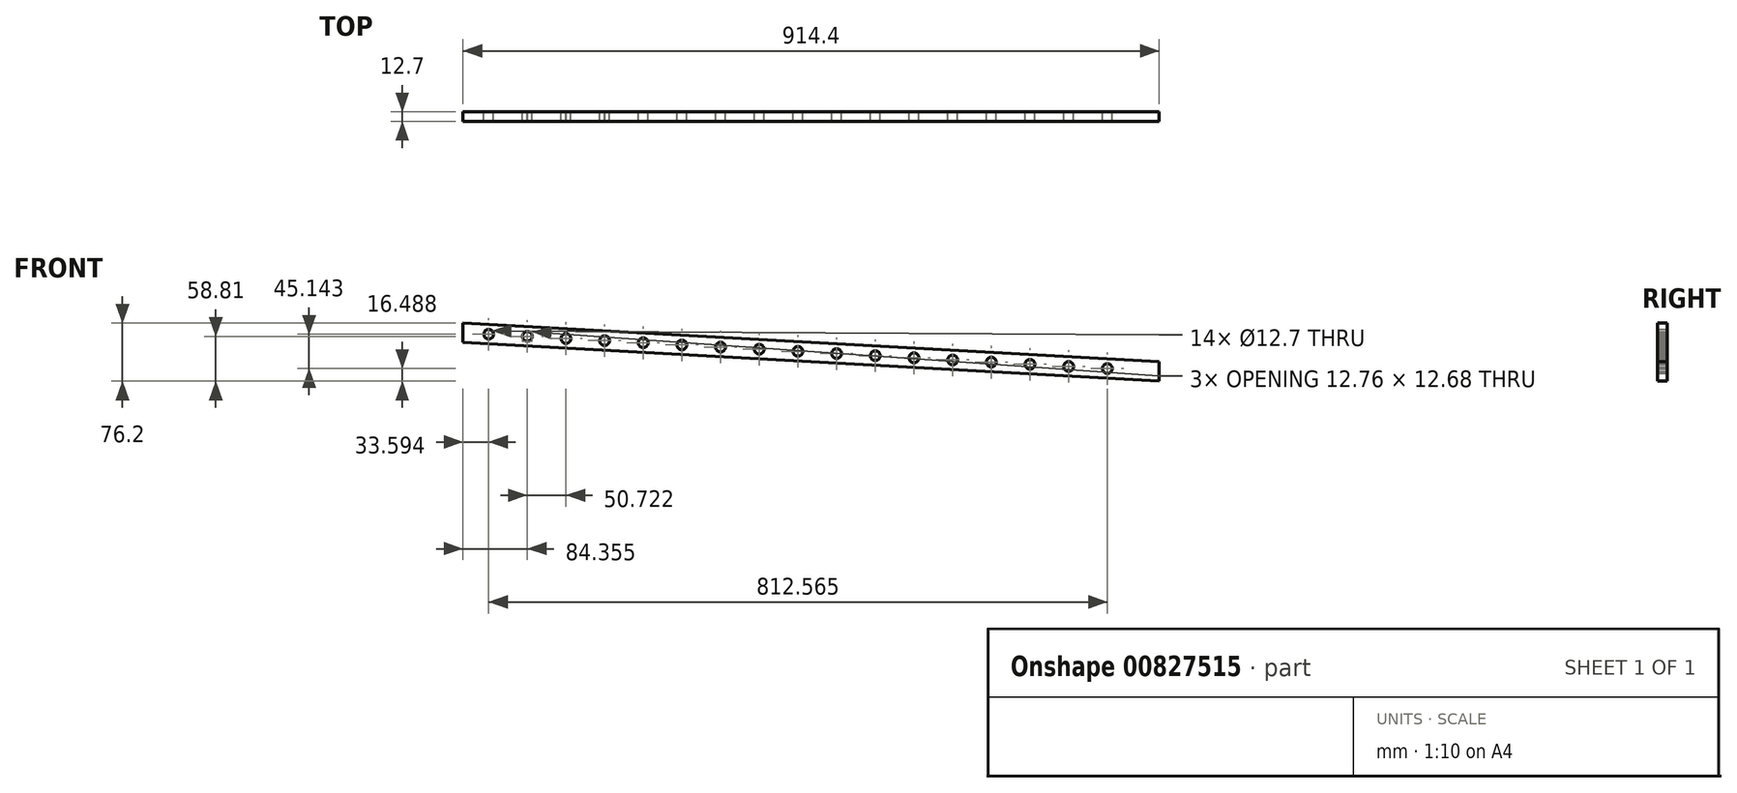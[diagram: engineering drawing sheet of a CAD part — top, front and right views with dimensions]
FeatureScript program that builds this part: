
annotation { "Feature Type Name" : "Feature", "Feature Type Description" : "" }
export const myFeature = defineFeature(function(context is Context, id is Id, definition is map)
    precondition{}
    {
        {
            var Q0;
            Q0=qCreatedBy(makeId("Front.planeOp"),FACE);
            var sketch = newSketch(context, id + "F0", { "sketchPlane" : qUnion([Q0])});
            skLineSegment(sketch, "E0", {"start": v(-457.2, 970.77) * mm, "end": v(-457.2, -45.23) * mm, "construction": true});
            skLineSegment(sketch, "E1", {"start": v(457.2, -45.23) * mm, "end": v(457.2, 919.97) * mm, "construction": true});
            skLineSegment(sketch, "E2", {"start": v(-457.2, 970.77) * mm, "end": v(457.2, 919.97) * mm});
            skLineSegment(sketch, "E3", {"start": v(-457.2, 945.37) * mm, "end": v(457.2, 894.57) * mm});
            skLineSegment(sketch, "E4", {"start": v(457.2, 919.97) * mm, "end": v(457.2, 894.57) * mm});
            skLineSegment(sketch, "E5", {"start": v(-457.2, 970.77) * mm, "end": v(-457.2, 945.37) * mm});
            skLineSegment(sketch, "E6", {"start": v(-457.2, 958.07) * mm, "end": v(457.2, 907.27) * mm, "construction": true});
            skCircle(sketch, "E7", {"center": v(-423.6, 956.2) * mm, "radius": 6.35 * mm});
            skCircle(sketch, "E8", {"center": v(-372.8, 953.38) * mm, "radius": 6.35 * mm});
            skCircle(sketch, "E9", {"center": v(-372.88, 953.38) * mm, "radius": 6.35 * mm});
            skCircle(sketch, "E10", {"center": v(-322.08, 950.56) * mm, "radius": 6.35 * mm});
            skCircle(sketch, "E11", {"center": v(-322.16, 950.56) * mm, "radius": 6.35 * mm});
            skCircle(sketch, "E12", {"center": v(-271.36, 947.74) * mm, "radius": 6.35 * mm});
            skCircle(sketch, "E13", {"center": v(-271.44, 947.75) * mm, "radius": 6.35 * mm});
            skCircle(sketch, "E14", {"center": v(-220.64, 944.92) * mm, "radius": 6.35 * mm});
            skCircle(sketch, "E15", {"center": v(-169.84, 942.1) * mm, "radius": 6.35 * mm});
            skCircle(sketch, "E16", {"center": v(-119.04, 939.28) * mm, "radius": 6.35 * mm});
            skCircle(sketch, "E17", {"center": v(-68.24, 936.46) * mm, "radius": 6.35 * mm});
            skCircle(sketch, "E18", {"center": v(-17.44, 933.64) * mm, "radius": 6.35 * mm});
            skCircle(sketch, "E19", {"center": v(33.36, 930.81) * mm, "radius": 6.35 * mm});
            skCircle(sketch, "E20", {"center": v(84.16, 928) * mm, "radius": 6.35 * mm});
            skCircle(sketch, "E21", {"center": v(134.96, 925.17) * mm, "radius": 6.35 * mm});
            skCircle(sketch, "E22", {"center": v(185.76, 922.35) * mm, "radius": 6.35 * mm});
            skCircle(sketch, "E23", {"center": v(236.56, 919.52) * mm, "radius": 6.35 * mm});
            skCircle(sketch, "E24", {"center": v(287.36, 916.7) * mm, "radius": 6.35 * mm});
            skCircle(sketch, "E25", {"center": v(338.16, 913.88) * mm, "radius": 6.35 * mm});
            skCircle(sketch, "E26", {"center": v(388.96, 911.06) * mm, "radius": 6.35 * mm});
            skCircle(sketch, "E27", {"center": v(490.56, 905.41) * mm, "radius": 6.35 * mm});
            skCircle(sketch, "E28", {"center": v(541.36, 902.6) * mm, "radius": 6.35 * mm});
            skCircle(sketch, "E29", {"center": v(592.16, 899.77) * mm, "radius": 6.35 * mm});
            skCircle(sketch, "E30", {"center": v(642.96, 896.95) * mm, "radius": 6.35 * mm});
            skCircle(sketch, "E31", {"center": v(693.76, 894.12) * mm, "radius": 6.35 * mm});
            skCircle(sketch, "E32", {"center": v(744.56, 891.3) * mm, "radius": 6.35 * mm});
            skCircle(sketch, "E33", {"center": v(795.36, 888.48) * mm, "radius": 6.35 * mm});
            skCircle(sketch, "E34", {"center": v(846.16, 885.66) * mm, "radius": 6.35 * mm});
            skCircle(sketch, "E35", {"center": v(896.96, 882.84) * mm, "radius": 6.35 * mm});
            skCircle(sketch, "E36", {"center": v(947.76, 880.01) * mm, "radius": 6.35 * mm});
            skCircle(sketch, "E37", {"center": v(998.56, 877.2) * mm, "radius": 6.35 * mm});
            skCircle(sketch, "E38", {"center": v(1049.36, 874.37) * mm, "radius": 6.35 * mm});
            skCircle(sketch, "E39", {"center": v(1100.16, 871.55) * mm, "radius": 6.82 * mm});
            skSolve(sketch);
        }
        {
            var Q0;
            Q0=makeQuery(id+"F0.imprint","IMPRINT",FACE,{"disambiguationData":[TD([[makeQuery(id+"F0.imprint","IMPRINT",EDGE,{"derivedFrom":sQuery(id+"F0.wireOp",EDGE,"E2")}),-1.0]])]});
            extrude(context, id + "F1", {"entities" : qUnion([Q0]), "depth" : 12.7 * mm, "offsetDistance" : 25.4 * mm});
        }
    });
